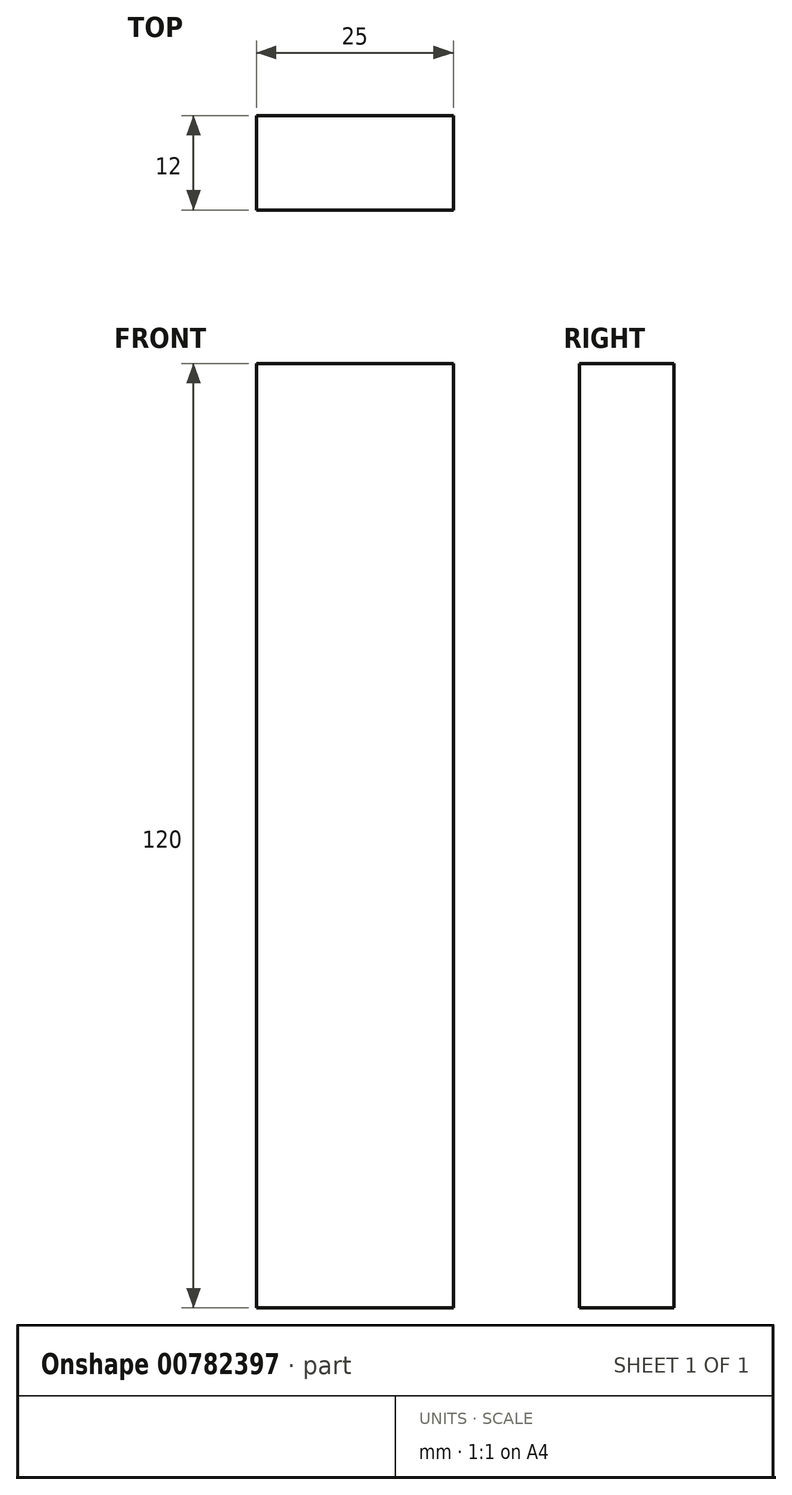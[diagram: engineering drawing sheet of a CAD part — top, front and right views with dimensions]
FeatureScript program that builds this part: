
annotation { "Feature Type Name" : "Feature", "Feature Type Description" : "" }
export const myFeature = defineFeature(function(context is Context, id is Id, definition is map)
    precondition{}
    {
        {
            var Q0;
            Q0=qCreatedBy(makeId("Front.planeOp"),FACE);
            var sketch = newSketch(context, id + "F0", { "sketchPlane" : qUnion([Q0])});
            skLineSegment(sketch, "E0.bottom", {"start": v(0, 0) * mm, "end": v(-25, 0) * mm});
            skLineSegment(sketch, "E0.top", {"start": v(0, 120) * mm, "end": v(-25, 120) * mm});
            skLineSegment(sketch, "E0.left", {"start": v(0, 0) * mm, "end": v(0, 120) * mm});
            skLineSegment(sketch, "E0.right", {"start": v(-25, 0) * mm, "end": v(-25, 120) * mm});
            skSolve(sketch);
        }
        {
            var Q0;
            Q0=makeQuery(id+"F0.imprint","IMPRINT",FACE,{"disambiguationData":[TD([[makeQuery(id+"F0.imprint","IMPRINT",EDGE,{"derivedFrom":sQuery(id+"F0.wireOp",EDGE,"E0.bottom")}),-1.0]])]});
            extrude(context, id + "F1", {"entities" : qUnion([Q0]), "depth" : 12 * mm, "offsetDistance" : 25 * mm});
        }
    });
